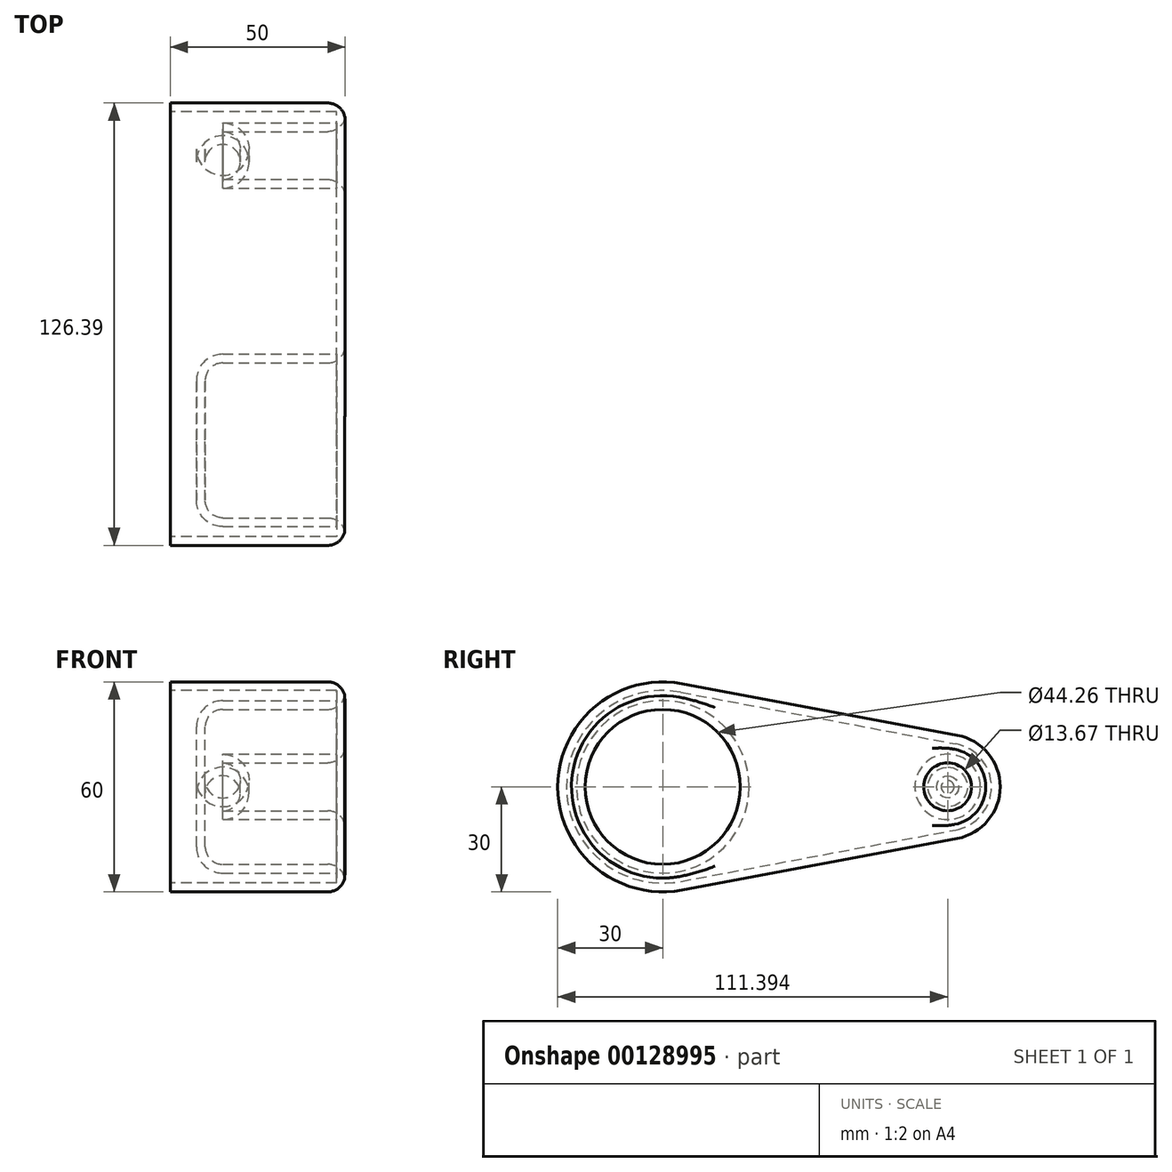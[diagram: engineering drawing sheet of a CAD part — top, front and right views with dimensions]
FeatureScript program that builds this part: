
annotation { "Feature Type Name" : "Feature", "Feature Type Description" : "" }
export const myFeature = defineFeature(function(context is Context, id is Id, definition is map)
    precondition{}
    {
        {
            var Q0;
            Q0=qCreatedBy(makeId("Right.planeOp"),FACE);
            var sketch = newSketch(context, id + "F4", { "sketchPlane" : qUnion([Q0])});
            skCircle(sketch, "E0", {"center": v(0, 0) * mm, "radius": 30 * mm});
            skCircle(sketch, "E1", {"center": v(81.4, 0) * mm, "radius": 15 * mm});
            skLineSegment(sketch, "E2", {"start": v(5.53, 29.49) * mm, "end": v(84.16, 14.74) * mm});
            skLineSegment(sketch, "E3", {"start": v(5.53, -29.49) * mm, "end": v(84.16, -14.74) * mm});
            skSolve(sketch);
        }
        {
            var Q0;
            {var subQ0=sQuery(id+"F4.wireOp",EDGE,"E2");Q0=makeQuery(id+"F4.imprint","IMPRINT",FACE,{"disambiguationData":[TD([[makeQuery(id+"F4.imprint","IMPRINT",EDGE,{"derivedFrom":subQ0}),-1.0]])]});}
            var Q1;
            Q1=sQuery(id+"F4.wireOp",EDGE,"E1");
            var Q2;
            Q2=sQuery(id+"F4.wireOp",EDGE,"E0");
            extrude(context, id + "F5", {"entities" : qUnion([Q0]), "bodyType" : ToolBodyType.SURFACE, "surfaceEntities" : qUnion([Q1, Q2]), "endBound" : BoundingType.SYMMETRIC, "depth" : 50 * mm});
        }
        {
            var Q0;
            {var subQ0=sQuery(id+"F4.wireOp",EDGE,"E0");var subQ1=makeQuery(id+"F4.imprint","INTERSECT",VERTEX,{"derivedFrom":[subQ0,sQuery(id+"F4.wireOp",EDGE,"E2")]});Q0=makeQuery(id+"F4.imprint","IMPRINT",FACE,{"disambiguationData":[TD([[makeQuery(id+"F4.imprint","IMPRINT",EDGE,{"disambiguationData":[TD([[subQ1,-1.0]])],"derivedFrom":subQ0}),1.0]])]});}
            var Q1;
            {var subQ0=sQuery(id+"F4.wireOp",EDGE,"E2");Q1=makeQuery(id+"F4.imprint","IMPRINT",FACE,{"disambiguationData":[TD([[makeQuery(id+"F4.imprint","IMPRINT",EDGE,{"derivedFrom":subQ0}),-1.0]])]});}
            var Q2;
            {var subQ0=sQuery(id+"F4.wireOp",EDGE,"E1");var subQ1=makeQuery(id+"F4.imprint","INTERSECT",VERTEX,{"derivedFrom":[subQ0,sQuery(id+"F4.wireOp",EDGE,"E2")]});Q2=makeQuery(id+"F4.imprint","IMPRINT",FACE,{"disambiguationData":[TD([[makeQuery(id+"F4.imprint","IMPRINT",EDGE,{"disambiguationData":[TD([[subQ1,-1.0]])],"derivedFrom":subQ0}),1.0]])]});}
            extrude(context, id + "F0", {"entities" : qUnion([Q0, Q1, Q2]), "depth" : 50 * mm});
        }
        {
            var Q0;
            Q0=makeQuery(id+"F0.opExtrude","CAP_FACE",FACE,{"disambiguationData":[OSD([sQuery(id+"F4.wireOp",EDGE,"E0"),sQuery(id+"F4.wireOp",EDGE,"E1"),sQuery(id+"F4.wireOp",EDGE,"E2"),sQuery(id+"F4.wireOp",EDGE,"E3")])],"isStart":false});
            var sketch = newSketch(context, id + "F6", { "sketchPlane" : qUnion([Q0])});
            skCircle(sketch, "E4", {"center": v(0, 0) * mm, "radius": 22.13 * mm});
            skCircle(sketch, "E5", {"center": v(81.4, 0) * mm, "radius": 6.84 * mm});
            skSolve(sketch);
        }
        {
            var Q0;
            Q0=makeQuery(id+"F6.imprint","IMPRINT",FACE,{"disambiguationData":[TD([[makeQuery(id+"F6.imprint","IMPRINT",EDGE,{"derivedFrom":sQuery(id+"F6.wireOp",EDGE,"E4")}),1.0]])]});
            var Q1;
            Q1=makeQuery(id+"F6.imprint","IMPRINT",FACE,{"disambiguationData":[TD([[makeQuery(id+"F6.imprint","IMPRINT",EDGE,{"derivedFrom":sQuery(id+"F6.wireOp",EDGE,"E5")}),1.0]])]});
            extrude(context, id + "F7", {"entities" : qUnion([Q0, Q1]), "operationType" : NewBodyOperationType.REMOVE, "oppositeDirection" : true, "depth" : 40 * mm});
        }
        {
            var Q0;
            Q0=makeQuery(id+"F7.boolean.opBoolean","COPY",FACE,{"derivedFrom":makeQuery(id+"F7.opExtrude","CAP_FACE",FACE,{"disambiguationData":[OSD([sQuery(id+"F6.wireOp",EDGE,"E4")])],"isStart":false})});
            var Q1;
            Q1=makeQuery(id+"F7.boolean.opBoolean","COPY",FACE,{"derivedFrom":makeQuery(id+"F7.opExtrude","CAP_FACE",FACE,{"disambiguationData":[OSD([sQuery(id+"F6.wireOp",EDGE,"E5")])],"isStart":false})});
            var Q2;
            Q2=makeQuery(id+"F7.boolean.opBoolean","COPY",EDGE,{"derivedFrom":makeQuery(id+"F7.opExtrude","CAP_EDGE",EDGE,{"disambiguationData":[OSD([sQuery(id+"F6.wireOp",EDGE,"E5")])],"isStart":true})});
            var Q3;
            Q3=makeQuery(id+"F7.boolean.opBoolean","COPY",EDGE,{"derivedFrom":makeQuery(id+"F7.opExtrude","CAP_EDGE",EDGE,{"disambiguationData":[OSD([sQuery(id+"F6.wireOp",EDGE,"E4")])],"isStart":true})});
            fillet(context, id + "F1", {"entities" : qUnion([Q0, Q1, Q2, Q3]), "radius" : 5 * mm, "tangentPropagation" : true, "allowEdgeOverflow" : false});
        }
        {
            var Q0;
            Q0=makeQuery(id+"F0.opExtrude","CAP_FACE",FACE,{"disambiguationData":[OSD([sQuery(id+"F4.wireOp",EDGE,"E0"),sQuery(id+"F4.wireOp",EDGE,"E1"),sQuery(id+"F4.wireOp",EDGE,"E2"),sQuery(id+"F4.wireOp",EDGE,"E3")])],"isStart":true});
            var Q1;
            Q1=makeQuery(id+"F0.opExtrude","SWEPT_BODY",BODY,{"disambiguationData":[OSD([sQuery(id+"F4.wireOp",EDGE,"E0"),sQuery(id+"F4.wireOp",EDGE,"E1"),sQuery(id+"F4.wireOp",EDGE,"E2"),sQuery(id+"F4.wireOp",EDGE,"E3")])]});
            shell(context, id + "F2", {"entities" : qUnion([Q0]), "parts" : qUnion([Q1]), "thickness" : 2.5 * mm});
        }
        {
            var Q0;
            Q0=makeQuery(id+"F0.opExtrude","CAP_FACE",FACE,{"disambiguationData":[OSD([sQuery(id+"F4.wireOp",EDGE,"E0"),sQuery(id+"F4.wireOp",EDGE,"E1"),sQuery(id+"F4.wireOp",EDGE,"E2"),sQuery(id+"F4.wireOp",EDGE,"E3")])],"isStart":false});
            fillet(context, id + "F3", {"entities" : qUnion([Q0]), "radius" : 5 * mm, "tangentPropagation" : true, "allowEdgeOverflow" : false});
        }
    });
